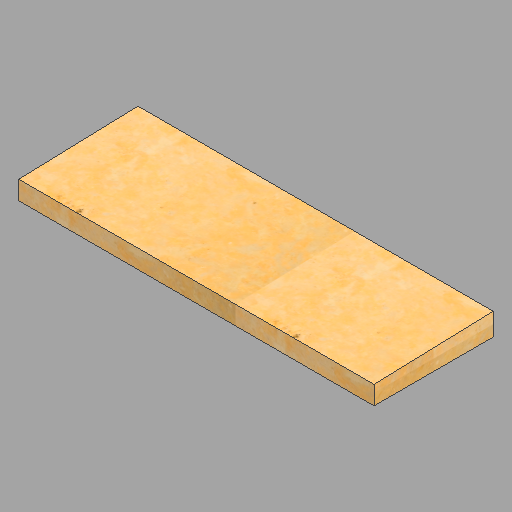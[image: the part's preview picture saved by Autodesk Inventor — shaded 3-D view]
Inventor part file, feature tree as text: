
AUTODESK INVENTOR PART (.ipt)
format: ipt  version: 2023 (Build 270158030, 158C)  size: 231,424 bytes
history: native  units: in
note: dims shown in document units (in); Inventor stores cm internally (conversion verified against a paired STEP export)
features: extrude x2, sketch x2
ambient origin geometry x8: Origin, YZ Plane, XZ Plane, XY Plane, X Axis, Y Axis, Z Axis, Center Point
bodies: Solid1 (feature_tree)
feature tree (4):
  extrude  "Extrusion1"  Depth=16.0in
  extrude  "Extrusion2"  Depth=47.6875in TaperAngle=0.0deg
  sketch  "Sketch1"  dims[d0=3.0in d1=16.0in]
  sketch  "Sketch2"  dims[d2=2.5in d3=47.6875in d4=0.0in d5=7.375in d6=32.0in d7=0.375in d8=0.375in d9=1.5in d10=0.0in]
